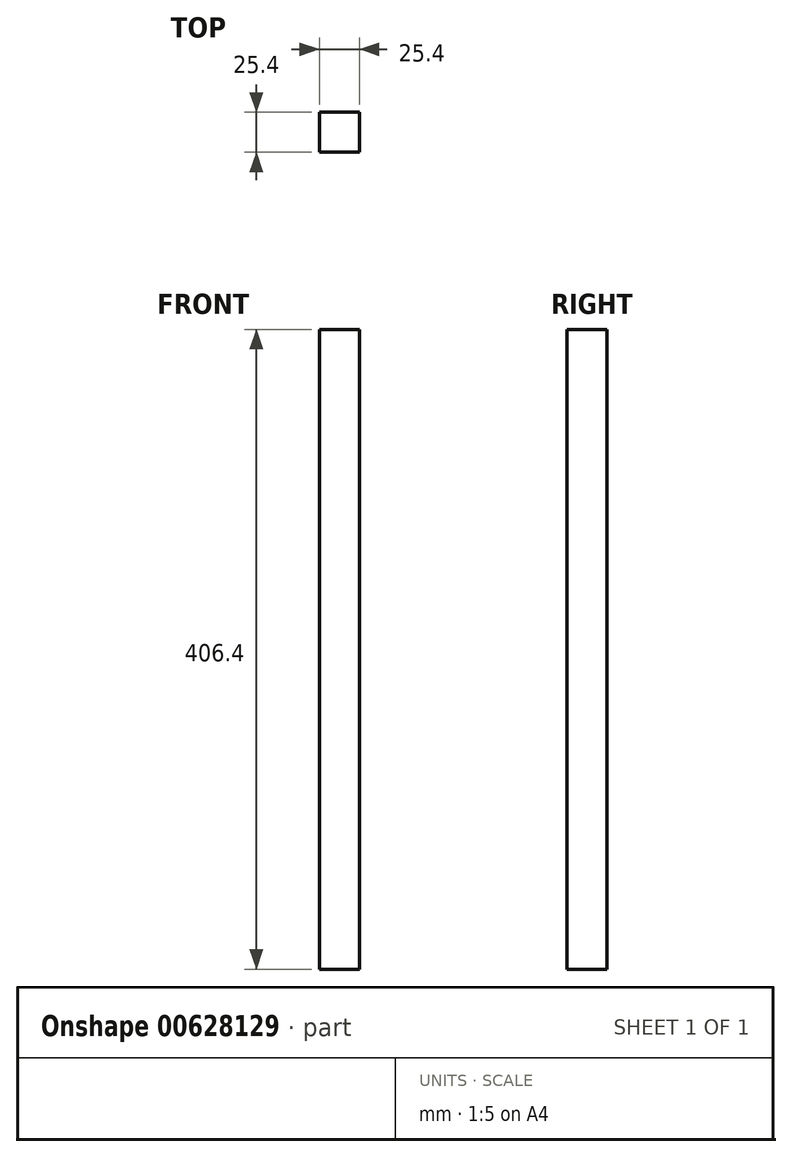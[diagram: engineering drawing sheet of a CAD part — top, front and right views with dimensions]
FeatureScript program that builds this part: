
annotation { "Feature Type Name" : "Feature", "Feature Type Description" : "" }
export const myFeature = defineFeature(function(context is Context, id is Id, definition is map)
    precondition{}
    {
        {
            var Q0;
            Q0=qCreatedBy(makeId("Top.planeOp"),FACE);
            var sketch = newSketch(context, id + "F0", { "sketchPlane" : qUnion([Q0])});
            skLineSegment(sketch, "E0.bottom", {"start": v(12.7, 12.7) * mm, "end": v(-12.7, 12.7) * mm});
            skLineSegment(sketch, "E0.top", {"start": v(12.7, -12.7) * mm, "end": v(-12.7, -12.7) * mm});
            skLineSegment(sketch, "E0.left", {"start": v(12.7, 12.7) * mm, "end": v(12.7, -12.7) * mm});
            skLineSegment(sketch, "E0.right", {"start": v(-12.7, 12.7) * mm, "end": v(-12.7, -12.7) * mm});
            skPoint(sketch, "E0.middle", {"position": v(0, 0) * mm});
            skSolve(sketch);
        }
        {
            var Q0;
            Q0=makeQuery(id+"F0.imprint","IMPRINT",FACE,{"disambiguationData":[TD([[makeQuery(id+"F0.imprint","IMPRINT",EDGE,{"derivedFrom":sQuery(id+"F0.wireOp",EDGE,"E0.bottom")}),1.0]])]});
            extrude(context, id + "F1", {"entities" : qUnion([Q0]), "depth" : 406.4 * mm, "offsetDistance" : 25.4 * mm});
        }
    });
